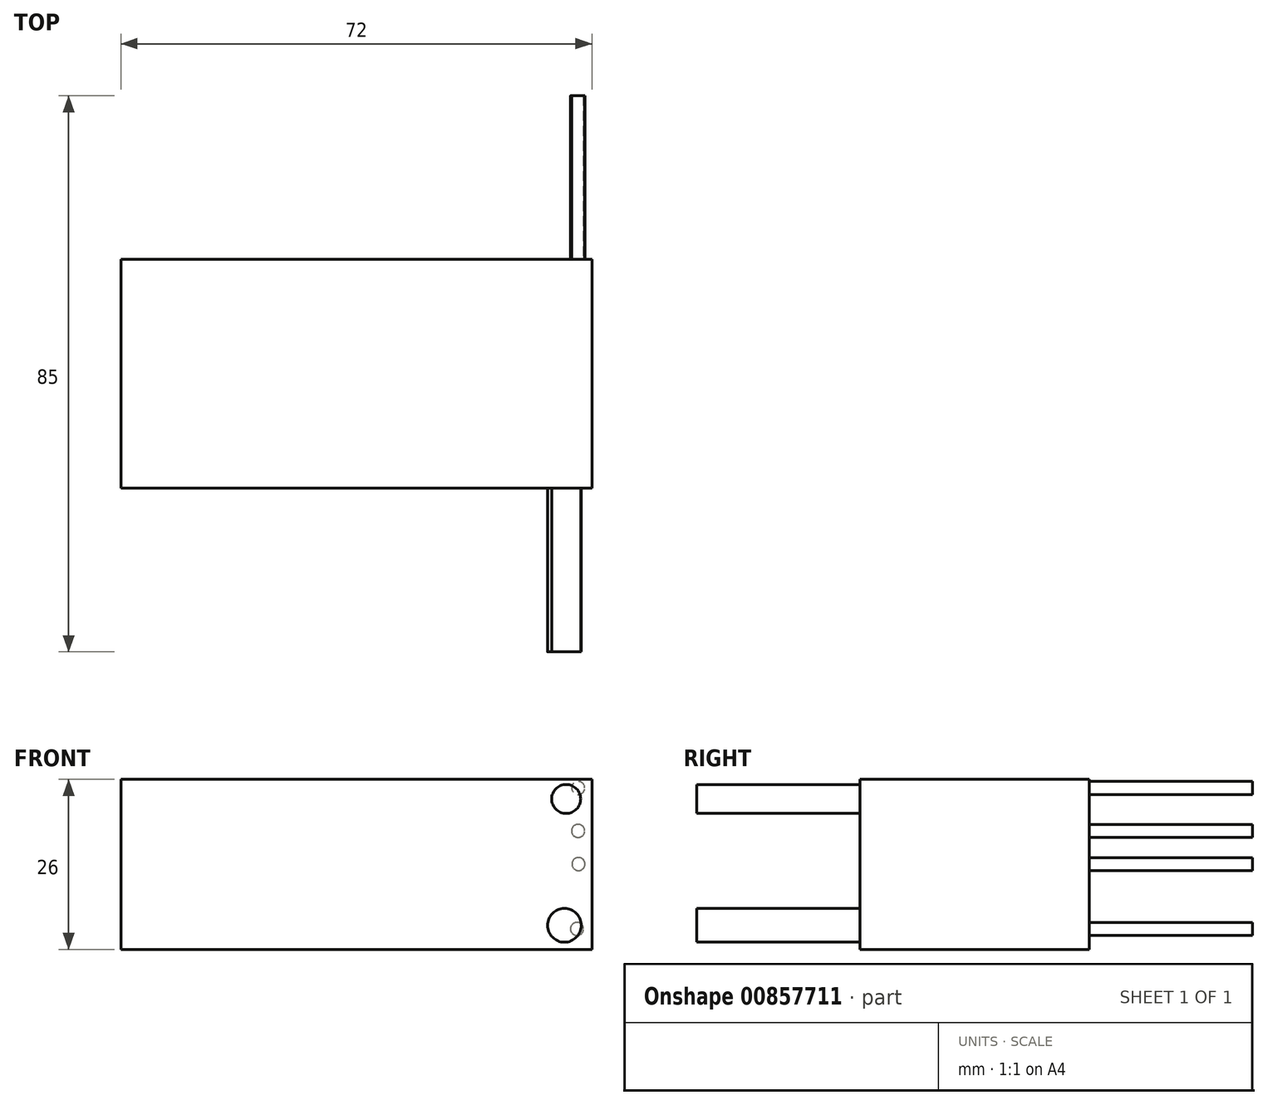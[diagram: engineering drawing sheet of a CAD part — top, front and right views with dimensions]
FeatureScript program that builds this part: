
annotation { "Feature Type Name" : "Feature", "Feature Type Description" : "" }
export const myFeature = defineFeature(function(context is Context, id is Id, definition is map)
    precondition{}
    {
        {
            var Q0;
            Q0=qCreatedBy(makeId("Top.planeOp"),FACE);
            var sketch = newSketch(context, id + "F0", { "sketchPlane" : qUnion([Q0])});
            skLineSegment(sketch, "E0.bottom", {"start": v(36, 17.5) * mm, "end": v(-36, 17.5) * mm});
            skLineSegment(sketch, "E0.top", {"start": v(36, -17.5) * mm, "end": v(-36, -17.5) * mm});
            skLineSegment(sketch, "E0.left", {"start": v(36, 17.5) * mm, "end": v(36, -17.5) * mm});
            skLineSegment(sketch, "E0.right", {"start": v(-36, 17.5) * mm, "end": v(-36, -17.5) * mm});
            skPoint(sketch, "E0.middle", {"position": v(0, 0) * mm});
            skSolve(sketch);
        }
        {
            var Q0;
            Q0=makeQuery(id+"F0.imprint","IMPRINT",FACE,{"disambiguationData":[TD([[makeQuery(id+"F0.imprint","IMPRINT",EDGE,{"derivedFrom":sQuery(id+"F0.wireOp",EDGE,"E0.bottom")}),1.0]])]});
            extrude(context, id + "F1", {"entities" : qUnion([Q0]), "depth" : 26 * mm, "offsetDistance" : 25 * mm});
        }
        {
            var Q0;
            Q0=makeQuery(id+"F1.opExtrude","SWEPT_FACE",FACE,{"disambiguationData":[OSD([sQuery(id+"F0.wireOp",EDGE,"E0.top")])]});
            var sketch = newSketch(context, id + "F2", { "sketchPlane" : qUnion([Q0])});
            skCircle(sketch, "E1", {"center": v(32.06, 23) * mm, "radius": 2.22 * mm});
            skCircle(sketch, "E2", {"center": v(31.8, 3.68) * mm, "radius": 2.58 * mm});
            skSolve(sketch);
        }
        {
            var Q0;
            Q0=makeQuery(id+"F2.imprint","IMPRINT",FACE,{"disambiguationData":[TD([[makeQuery(id+"F2.imprint","IMPRINT",EDGE,{"derivedFrom":sQuery(id+"F2.wireOp",EDGE,"E1")}),1.0]])]});
            var Q1;
            Q1=makeQuery(id+"F2.imprint","IMPRINT",FACE,{"disambiguationData":[TD([[makeQuery(id+"F2.imprint","IMPRINT",EDGE,{"derivedFrom":sQuery(id+"F2.wireOp",EDGE,"E2")}),1.0]])]});
            extrude(context, id + "F3", {"entities" : qUnion([Q0, Q1]), "operationType" : NewBodyOperationType.ADD, "depth" : 25 * mm, "offsetDistance" : 25 * mm});
        }
        {
            var Q0;
            Q0=makeQuery(id+"F1.opExtrude","SWEPT_FACE",FACE,{"disambiguationData":[OSD([sQuery(id+"F0.wireOp",EDGE,"E0.bottom")])]});
            var sketch = newSketch(context, id + "F4", { "sketchPlane" : qUnion([Q0])});
            skCircle(sketch, "E3", {"center": v(-33.89, 24.68) * mm, "radius": 1 * mm});
            skCircle(sketch, "E4", {"center": v(-33.88, 18.11) * mm, "radius": 1 * mm});
            skCircle(sketch, "E5", {"center": v(-33.94, 13.04) * mm, "radius": 1 * mm});
            skCircle(sketch, "E6", {"center": v(-33.7, 3.12) * mm, "radius": 1 * mm});
            skSolve(sketch);
        }
        {
            var Q0;
            Q0 = qSketchRegion(id + "F4", true);
            extrude(context, id + "F5", {"entities" : qUnion([Q0]), "operationType" : NewBodyOperationType.ADD, "depth" : 25 * mm, "offsetDistance" : 25 * mm});
        }
    });
